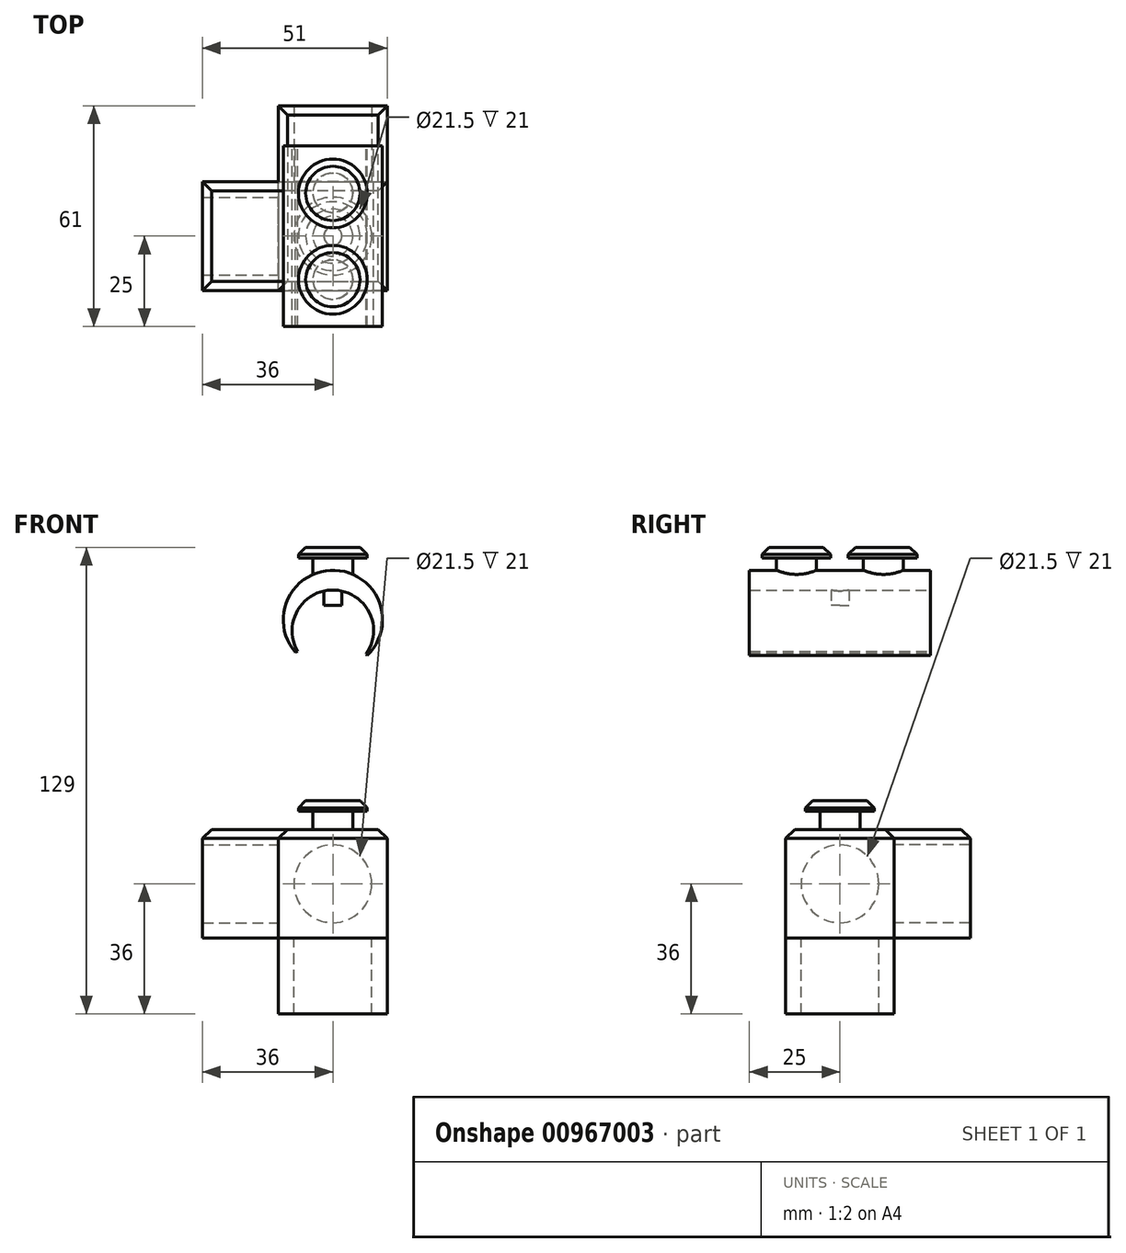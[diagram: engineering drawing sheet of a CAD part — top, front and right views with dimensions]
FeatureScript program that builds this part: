
annotation { "Feature Type Name" : "Feature", "Feature Type Description" : "" }
export const myFeature = defineFeature(function(context is Context, id is Id, definition is map)
    precondition{}
    {
        {
            var Q0;
            Q0=qCreatedBy(makeId("Front.planeOp"),FACE);
            var sketch = newSketch(context, id + "F0", { "sketchPlane" : qUnion([Q0])});
            skLineSegment(sketch, "E0.bottom", {"start": v(-15, 15) * mm, "end": v(15, 15) * mm});
            skLineSegment(sketch, "E0.top", {"start": v(-15, -15) * mm, "end": v(15, -15) * mm});
            skLineSegment(sketch, "E0.left", {"start": v(-15, 15) * mm, "end": v(-15, -15) * mm});
            skLineSegment(sketch, "E0.right", {"start": v(15, 15) * mm, "end": v(15, -15) * mm});
            skPoint(sketch, "E0.middle", {"position": v(0, 0) * mm});
            skLineSegment(sketch, "E1", {"start": v(0, 17.66) * mm, "end": v(0, -29.16) * mm, "construction": true});
            skLineSegment(sketch, "E2", {"start": v(-17.14, 0) * mm, "end": v(20.18, 0) * mm, "construction": true});
            skLineSegment(sketch, "E3", {"start": v(43.79, 18.03) * mm, "end": v(43.79, -19.92) * mm, "construction": true});
            skSolve(sketch);
        }
        {
            var Q0;
            Q0=makeQuery(id+"F0.imprint","IMPRINT",FACE,{"disambiguationData":[TD([[makeQuery(id+"F0.imprint","IMPRINT",EDGE,{"derivedFrom":sQuery(id+"F0.wireOp",EDGE,"E0.bottom")}),-1.0]])]});
            extrude(context, id + "F1", {"entities" : qUnion([Q0]), "endBound" : BoundingType.SYMMETRIC, "depth" : 30 * mm, "offsetDistance" : 25 * mm});
        }
        {
            var Q0;
            Q0=qCreatedBy(makeId("Right.planeOp"),FACE);
            var sketch = newSketch(context, id + "F2", { "sketchPlane" : qUnion([Q0])});
            skLineSegment(sketch, "E4", {"start": v(40, 25.86) * mm, "end": v(40, -15.94) * mm, "construction": true});
            skSolve(sketch);
        }
        {
            var Q0;
            Q0=makeQuery(id+"F1.opExtrude","SWEPT_FACE",FACE,{"disambiguationData":[OSD([sQuery(id+"F0.wireOp",EDGE,"E0.left")])]});
            var sketch = newSketch(context, id + "F3", { "sketchPlane" : qUnion([Q0])});
            skCircle(sketch, "E5", {"center": v(0, 0) * mm, "radius": 10.75 * mm});
            skSolve(sketch);
        }
        {
            var Q0;
            Q0=makeQuery(id+"F3.imprint","IMPRINT",FACE,{"disambiguationData":[TD([[makeQuery(id+"F3.imprint","IMPRINT",EDGE,{"derivedFrom":sQuery(id+"F3.wireOp",EDGE,"E5")}),-1.0]])]});
            extrude(context, id + "F4", {"entities" : qUnion([Q0]), "operationType" : NewBodyOperationType.ADD, "depth" : 21 * mm, "offsetDistance" : 25 * mm});
        }
        {
            var Q0;
            Q0=makeQuery(id+"F1.opExtrude","SWEPT_BODY",BODY,{"disambiguationData":[OSD([sQuery(id+"F0.wireOp",EDGE,"E0.bottom"),sQuery(id+"F0.wireOp",EDGE,"E0.top"),sQuery(id+"F0.wireOp",EDGE,"E0.left"),sQuery(id+"F0.wireOp",EDGE,"E0.right")])]});
            var Q1;
            Q1=sQuery(id+"F0.wireOp",EDGE,"E1");
            circularPattern(context, id + "F5", {"entities" : qUnion([Q0]), "axis" : qUnion([Q1]), "angle" : 90 * degree, "instanceCount" : 2, "equalSpace" : true});
        }
        {
            var Q0;
            {var subQ0=sQuery(id+"F0.wireOp",EDGE,"E0.top");Q0=makeQuery(id+"F4.boolean.opBoolean","MERGE",FACE,{"derivedFrom":[makeQuery(id+"F1.opExtrude","SWEPT_FACE",FACE,{"disambiguationData":[OSD([subQ0])]}),makeQuery(id+"F4.opExtrude","SWEPT_FACE",FACE,{"disambiguationData":[OSD([subQ0,sQuery(id+"F0.wireOp",EDGE,"E0.left")])]})]});}
            var sketch = newSketch(context, id + "F6", { "sketchPlane" : qUnion([Q0])});
            skCircle(sketch, "E6", {"center": v(0, 0) * mm, "radius": 10.75 * mm});
            skLineSegment(sketch, "E7", {"start": v(-15, 15) * mm, "end": v(-15, -15) * mm});
            skSolve(sketch);
        }
        {
            var Q0;
            Q0=makeQuery(id+"F6.imprint","IMPRINT",FACE,{"disambiguationData":[TD([[makeQuery(id+"F6.imprint","IMPRINT",EDGE,{"derivedFrom":sQuery(id+"F6.wireOp",EDGE,"E6")}),-1.0]])]});
            extrude(context, id + "F7", {"entities" : qUnion([Q0]), "depth" : 21 * mm, "offsetDistance" : 25 * mm});
        }
        {
            var Q0;
            {var subQ0=sQuery(id+"F0.wireOp",EDGE,"E0.bottom");Q0=makeQuery(id+"F4.boolean.opBoolean","MERGE",FACE,{"derivedFrom":[makeQuery(id+"F1.opExtrude","SWEPT_FACE",FACE,{"disambiguationData":[OSD([subQ0])]}),makeQuery(id+"F4.opExtrude","SWEPT_FACE",FACE,{"disambiguationData":[OSD([subQ0,sQuery(id+"F0.wireOp",EDGE,"E0.left")])]})]});}
            cPlane(context, id + "F8", {"entities" : qUnion([Q0]), "cplaneType" : CPlaneType.OFFSET, "offset" : 5 * mm, "width" : 150 * mm, "height" : 150 * mm});
        }
        {
            var Q0;
            Q0=qCreatedBy(id+"F8.planeOp",FACE);
            var sketch = newSketch(context, id + "F9", { "sketchPlane" : qUnion([Q0])});
            skCircle(sketch, "E8", {"center": v(0, 0) * mm, "radius": 5.5 * mm});
            skSolve(sketch);
        }
        {
            var Q0;
            Q0=makeQuery(id+"F9.imprint","IMPRINT",FACE,{"disambiguationData":[TD([[makeQuery(id+"F9.imprint","IMPRINT",EDGE,{"derivedFrom":sQuery(id+"F9.wireOp",EDGE,"E8")}),1.0]])]});
            extrude(context, id + "F10", {"entities" : qUnion([Q0]), "oppositeDirection" : true, "depth" : 5 * mm, "offsetDistance" : 25 * mm});
        }
        {
            var Q0;
            Q0=makeQuery(id+"F10.opExtrude","CAP_FACE",FACE,{"disambiguationData":[OSD([sQuery(id+"F9.wireOp",EDGE,"E8")])],"isStart":true});
            var sketch = newSketch(context, id + "F11", { "sketchPlane" : qUnion([Q0])});
            skCircle(sketch, "E9", {"center": v(0, 0) * mm, "radius": 9.5 * mm});
            skSolve(sketch);
        }
        {
            var Q0;
            Q0=makeQuery(id+"F11.imprint","IMPRINT",FACE,{"disambiguationData":[TD([[makeQuery(id+"F11.imprint","IMPRINT",EDGE,{"derivedFrom":sQuery(id+"F11.wireOp",EDGE,"E9")}),1.0]])]});
            var Q1;
            Q1=makeQuery(id+"F11.imprint","IMPRINT",FACE,{"disambiguationData":[TD([[makeQuery(id+"F11.imprint","IMPRINT",EDGE,{"derivedFrom":makeQuery(id+"F10.opExtrude","CAP_EDGE",EDGE,{"disambiguationData":[OSD([sQuery(id+"F9.wireOp",EDGE,"E8")])],"isStart":true})}),1.0]])]});
            extrude(context, id + "F12", {"entities" : qUnion([Q0, Q1]), "depth" : 3 * mm, "offsetDistance" : 25 * mm});
        }
        {
            var Q0;
            Q0=makeQuery(id+"F12.opExtrude","CAP_EDGE",EDGE,{"disambiguationData":[OSD([sQuery(id+"F11.wireOp",EDGE,"E9")])],"isStart":false});
            chamfer(context, id + "F13", {"entities" : qUnion([Q0]), "width" : 2 * mm, "tangentPropagation" : true});
        }
        {
            var Q0;
            {var subQ0=sQuery(id+"F0.wireOp",EDGE,"E0.left");var subQ1=sQuery(id+"F0.wireOp",EDGE,"E0.bottom");Q0=makeQuery(id+"F5.opPattern","COPY",EDGE,{"derivedFrom":makeQuery(id+"F4.boolean.opBoolean","MERGE",EDGE,{"derivedFrom":[makeQuery(id+"F1.opExtrude","CAP_EDGE",EDGE,{"disambiguationData":[OSD([subQ1])],"isStart":true}),makeQuery(id+"F4.opExtrude","SWEPT_EDGE",EDGE,{"disambiguationData":[OSD([subQ1,subQ0]),TDD([makeQuery(id+"F3.imprint","INTERSECT",VERTEX,{"derivedFrom":[makeQuery(id+"F1.opExtrude","SWEPT_EDGE",EDGE,{"disambiguationData":[OSD([subQ1,subQ0])]}),makeQuery(id+"F1.opExtrude","CAP_EDGE",EDGE,{"disambiguationData":[OSD([subQ0])],"isStart":true})]})])]})]}),"instanceName":"1"});}
            var Q1;
            {var subQ0=sQuery(id+"F0.wireOp",EDGE,"E0.left");var subQ1=sQuery(id+"F0.wireOp",EDGE,"E0.bottom");Q1=makeQuery(id+"F4.boolean.opBoolean","MERGE",EDGE,{"derivedFrom":[makeQuery(id+"F1.opExtrude","CAP_EDGE",EDGE,{"disambiguationData":[OSD([subQ1])],"isStart":false}),makeQuery(id+"F4.opExtrude","SWEPT_EDGE",EDGE,{"disambiguationData":[OSD([subQ1,subQ0]),TDD([makeQuery(id+"F3.imprint","INTERSECT",VERTEX,{"derivedFrom":[makeQuery(id+"F1.opExtrude","SWEPT_EDGE",EDGE,{"disambiguationData":[OSD([subQ1,subQ0])]}),makeQuery(id+"F1.opExtrude","CAP_EDGE",EDGE,{"disambiguationData":[OSD([subQ0])],"isStart":false})]})])]})]});}
            var Q2;
            Q2=makeQuery(id+"F5.opPattern","COPY",EDGE,{"derivedFrom":makeQuery(id+"F4.opExtrude","CAP_EDGE",EDGE,{"disambiguationData":[OSD([sQuery(id+"F0.wireOp",EDGE,"E0.bottom"),sQuery(id+"F0.wireOp",EDGE,"E0.left")])],"isStart":false}),"instanceName":"1"});
            var Q3;
            {var subQ0=sQuery(id+"F0.wireOp",EDGE,"E0.bottom");Q3=makeQuery(id+"F5.opPattern","COPY",FACE,{"derivedFrom":makeQuery(id+"F4.boolean.opBoolean","MERGE",FACE,{"derivedFrom":[makeQuery(id+"F1.opExtrude","SWEPT_FACE",FACE,{"disambiguationData":[OSD([subQ0])]}),makeQuery(id+"F4.opExtrude","SWEPT_FACE",FACE,{"disambiguationData":[OSD([subQ0,sQuery(id+"F0.wireOp",EDGE,"E0.left")])]})]}),"instanceName":"1"});}
            var Q4;
            {var subQ0=sQuery(id+"F0.wireOp",EDGE,"E0.left");var subQ1=sQuery(id+"F0.wireOp",EDGE,"E0.bottom");Q4=makeQuery(id+"F4.boolean.opBoolean","MERGE",EDGE,{"derivedFrom":[makeQuery(id+"F1.opExtrude","CAP_EDGE",EDGE,{"disambiguationData":[OSD([subQ1])],"isStart":true}),makeQuery(id+"F4.opExtrude","SWEPT_EDGE",EDGE,{"disambiguationData":[OSD([subQ1,subQ0]),TDD([makeQuery(id+"F3.imprint","INTERSECT",VERTEX,{"derivedFrom":[makeQuery(id+"F1.opExtrude","SWEPT_EDGE",EDGE,{"disambiguationData":[OSD([subQ1,subQ0])]}),makeQuery(id+"F1.opExtrude","CAP_EDGE",EDGE,{"disambiguationData":[OSD([subQ0])],"isStart":true})]})])]})]});}
            var Q5;
            {var subQ0=sQuery(id+"F0.wireOp",EDGE,"E0.bottom");Q5=makeQuery(id+"F4.boolean.opBoolean","MERGE",FACE,{"derivedFrom":[makeQuery(id+"F1.opExtrude","SWEPT_FACE",FACE,{"disambiguationData":[OSD([subQ0])]}),makeQuery(id+"F4.opExtrude","SWEPT_FACE",FACE,{"disambiguationData":[OSD([subQ0,sQuery(id+"F0.wireOp",EDGE,"E0.left")])]})]});}
            chamfer(context, id + "F14", {"entities" : qUnion([Q0, Q1, Q2, Q3, Q4, Q5]), "width" : 2.5 * mm, "tangentPropagation" : true});
        }
        {
            var Q0;
            Q0=qCreatedBy(makeId("Front.planeOp"),FACE);
            var sketch = newSketch(context, id + "F15", { "sketchPlane" : qUnion([Q0])});
            skArc(sketch, "E10", {"start": v(-7.2, 61.32) * mm, "mid": v(0, 81.2) * mm, "end": v(7.2, 61.32) * mm});
            skArc(sketch, "E11", {"start": v(7.2, 61.32) * mm, "mid": v(0, 86.66) * mm, "end": v(-7.2, 61.32) * mm});
            skLineSegment(sketch, "E12", {"start": v(-10.3, 63.94) * mm, "end": v(-9.69, 64.23) * mm});
            skLineSegment(sketch, "E13", {"start": v(9.2, 63.48) * mm, "end": v(9.47, 63.07) * mm});
            skSolve(sketch);
        }
        {
            var Q0;
            {var subQ0=sQuery(id+"F15.wireOp",EDGE,"E12");Q0=makeQuery(id+"F15.imprint","IMPRINT",FACE,{"disambiguationData":[TD([[makeQuery(id+"F15.imprint","IMPRINT",EDGE,{"derivedFrom":subQ0}),1.0]])]});}
            extrude(context, id + "F16", {"entities" : qUnion([Q0]), "endBound" : BoundingType.SYMMETRIC, "depth" : 50 * mm, "offsetDistance" : 25 * mm});
        }
        {
            var Q0;
            Q0=qCreatedBy(makeId("Top.planeOp"),FACE);
            cPlane(context, id + "F17", {"entities" : qUnion([Q0]), "cplaneType" : CPlaneType.OFFSET, "offset" : 77 * mm, "width" : 150 * mm, "height" : 150 * mm});
        }
        {
            var Q0;
            Q0=qCreatedBy(id+"F17.planeOp",FACE);
            var sketch = newSketch(context, id + "F18", { "sketchPlane" : qUnion([Q0])});
            skCircle(sketch, "E14", {"center": v(0, 0) * mm, "radius": 2.5 * mm});
            skSolve(sketch);
        }
        {
            var Q0;
            Q0=makeQuery(id+"F18.imprint","IMPRINT",FACE,{"disambiguationData":[TD([[makeQuery(id+"F18.imprint","IMPRINT",EDGE,{"derivedFrom":sQuery(id+"F18.wireOp",EDGE,"E14")}),1.0]])]});
            extrude(context, id + "F19", {"entities" : qUnion([Q0]), "operationType" : NewBodyOperationType.ADD, "depth" : 7 * mm, "offsetDistance" : 25 * mm});
        }
        {
            var Q0;
            Q0=qCreatedBy(makeId("Top.planeOp"),FACE);
            cPlane(context, id + "F20", {"entities" : qUnion([Q0]), "cplaneType" : CPlaneType.OFFSET, "offset" : 90 * mm, "width" : 150 * mm, "height" : 150 * mm});
        }
        {
            var Q0;
            Q0=qCreatedBy(id+"F20.planeOp",FACE);
            var sketch = newSketch(context, id + "F21", { "sketchPlane" : qUnion([Q0])});
            skCircle(sketch, "E15", {"center": v(0, 12) * mm, "radius": 5.5 * mm});
            skCircle(sketch, "E16", {"center": v(0, -12) * mm, "radius": 5.5 * mm});
            skSolve(sketch);
        }
        {
            var Q0;
            Q0=makeQuery(id+"F21.imprint","IMPRINT",FACE,{"disambiguationData":[TD([[makeQuery(id+"F21.imprint","IMPRINT",EDGE,{"derivedFrom":sQuery(id+"F21.wireOp",EDGE,"E15")}),1.0]])]});
            var Q1;
            Q1=makeQuery(id+"F21.imprint","IMPRINT",FACE,{"disambiguationData":[TD([[makeQuery(id+"F21.imprint","IMPRINT",EDGE,{"derivedFrom":sQuery(id+"F21.wireOp",EDGE,"E16")}),1.0]])]});
            extrude(context, id + "F22", {"entities" : qUnion([Q0, Q1]), "operationType" : NewBodyOperationType.ADD, "oppositeDirection" : true, "depth" : 5 * mm, "offsetDistance" : 25 * mm});
        }
        {
            var Q0;
            Q0=qCreatedBy(id+"F20.planeOp",FACE);
            var sketch = newSketch(context, id + "F23", { "sketchPlane" : qUnion([Q0])});
            skCircle(sketch, "E17", {"center": v(0, 11.8) * mm, "radius": 9.5 * mm});
            skCircle(sketch, "E18", {"center": v(0, -12.05) * mm, "radius": 9.5 * mm});
            skSolve(sketch);
        }
        {
            var Q0;
            Q0=makeQuery(id+"F23.imprint","IMPRINT",FACE,{"disambiguationData":[TD([[makeQuery(id+"F23.imprint","IMPRINT",EDGE,{"derivedFrom":sQuery(id+"F23.wireOp",EDGE,"E17")}),1.0]])]});
            var Q1;
            Q1=makeQuery(id+"F23.imprint","IMPRINT",FACE,{"disambiguationData":[TD([[makeQuery(id+"F23.imprint","IMPRINT",EDGE,{"derivedFrom":sQuery(id+"F23.wireOp",EDGE,"E18")}),1.0]])]});
            var Q2;
            Q2=makeQuery(id+"F21.imprint","IMPRINT",FACE,{"disambiguationData":[TD([[makeQuery(id+"F21.imprint","IMPRINT",EDGE,{"derivedFrom":sQuery(id+"F21.wireOp",EDGE,"E15")}),1.0]])]});
            var Q3;
            Q3=makeQuery(id+"F21.imprint","IMPRINT",FACE,{"disambiguationData":[TD([[makeQuery(id+"F21.imprint","IMPRINT",EDGE,{"derivedFrom":sQuery(id+"F21.wireOp",EDGE,"E16")}),1.0]])]});
            extrude(context, id + "F24", {"entities" : qUnion([Q0, Q1, Q2, Q3]), "operationType" : NewBodyOperationType.ADD, "depth" : 3 * mm, "offsetDistance" : 25 * mm});
        }
        {
            var Q0;
            Q0=makeQuery(id+"F24.opExtrude","CAP_EDGE",EDGE,{"disambiguationData":[OSD([sQuery(id+"F23.wireOp",EDGE,"E17")])],"isStart":false});
            var Q1;
            Q1=makeQuery(id+"F24.opExtrude","CAP_EDGE",EDGE,{"disambiguationData":[OSD([sQuery(id+"F23.wireOp",EDGE,"E18")])],"isStart":false});
            chamfer(context, id + "F25", {"entities" : qUnion([Q0, Q1]), "width" : 2 * mm, "tangentPropagation" : true});
        }
    });
